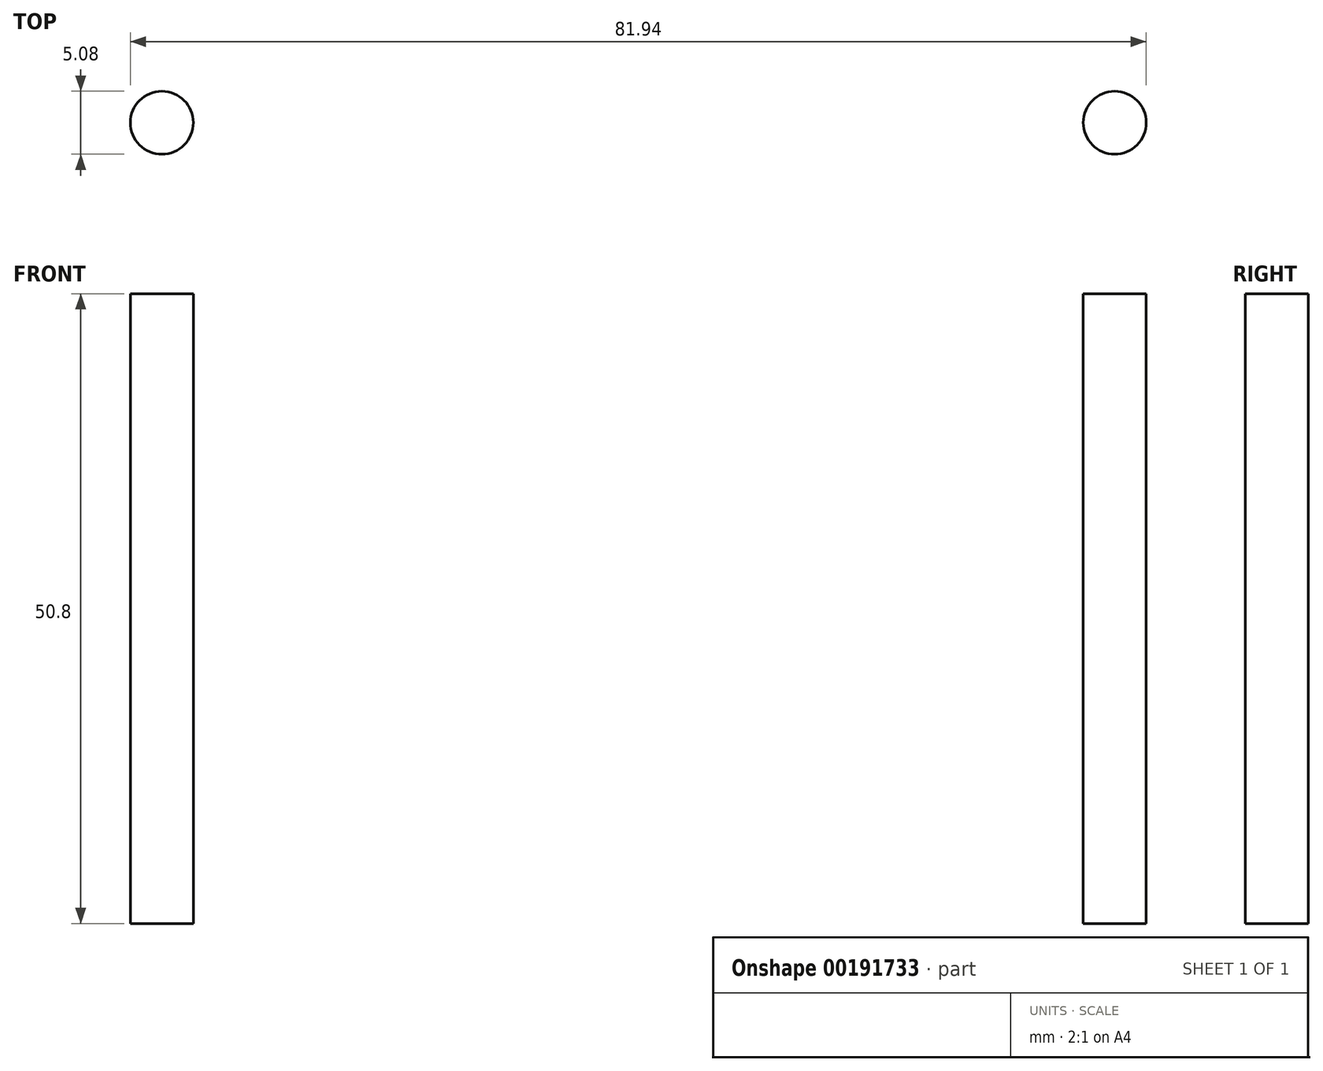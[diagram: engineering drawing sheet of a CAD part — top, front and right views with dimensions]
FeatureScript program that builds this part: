
annotation { "Feature Type Name" : "Feature", "Feature Type Description" : "" }
export const myFeature = defineFeature(function(context is Context, id is Id, definition is map)
    precondition{}
    {
        {
            var Q0;
            Q0=qCreatedBy(makeId("Front.planeOp"),FACE);
            var sketch = newSketch(context, id + "F0", { "sketchPlane" : qUnion([Q0])});
            skLineSegment(sketch, "E0", {"start": v(-38.43, 0) * mm, "end": v(-38.43, 50.8) * mm});
            skSolve(sketch);
        }
        {
            var Q0;
            Q0=qCreatedBy(makeId("Top.planeOp"),FACE);
            var sketch = newSketch(context, id + "F1", { "sketchPlane" : qUnion([Q0])});
            skCircle(sketch, "E1", {"center": v(-38.43, 0) * mm, "radius": 2.54 * mm});
            skSolve(sketch);
        }
        {
            var Q0;
            Q0 = qSketchRegion(id + "F1", true);
            var Q1;
            Q1 = qConstructionFilter(qBodyType(qCreatedBy(id + "F0" ,EDGE), BodyType.WIRE), ConstructionObject.NO);
            sweep(context, id + "F2", {"profiles" : qUnion([Q0]), "path" : qUnion([Q1])});
        }
        {
            var Q0;
            Q0=makeQuery(id+"F2.opSweep","SWEPT_BODY",BODY,{"disambiguationData":[OSD([sQuery(id+"F0.wireOp",EDGE,"E0"),sQuery(id+"F1.wireOp",EDGE,"E1")])]});
            var Q1;
            Q1=qCreatedBy(makeId("Right.planeOp"),FACE);
            mirror(context, id + "F3", {"entities" : qUnion([Q0]), "mirrorPlane" : qUnion([Q1])});
        }
    });
